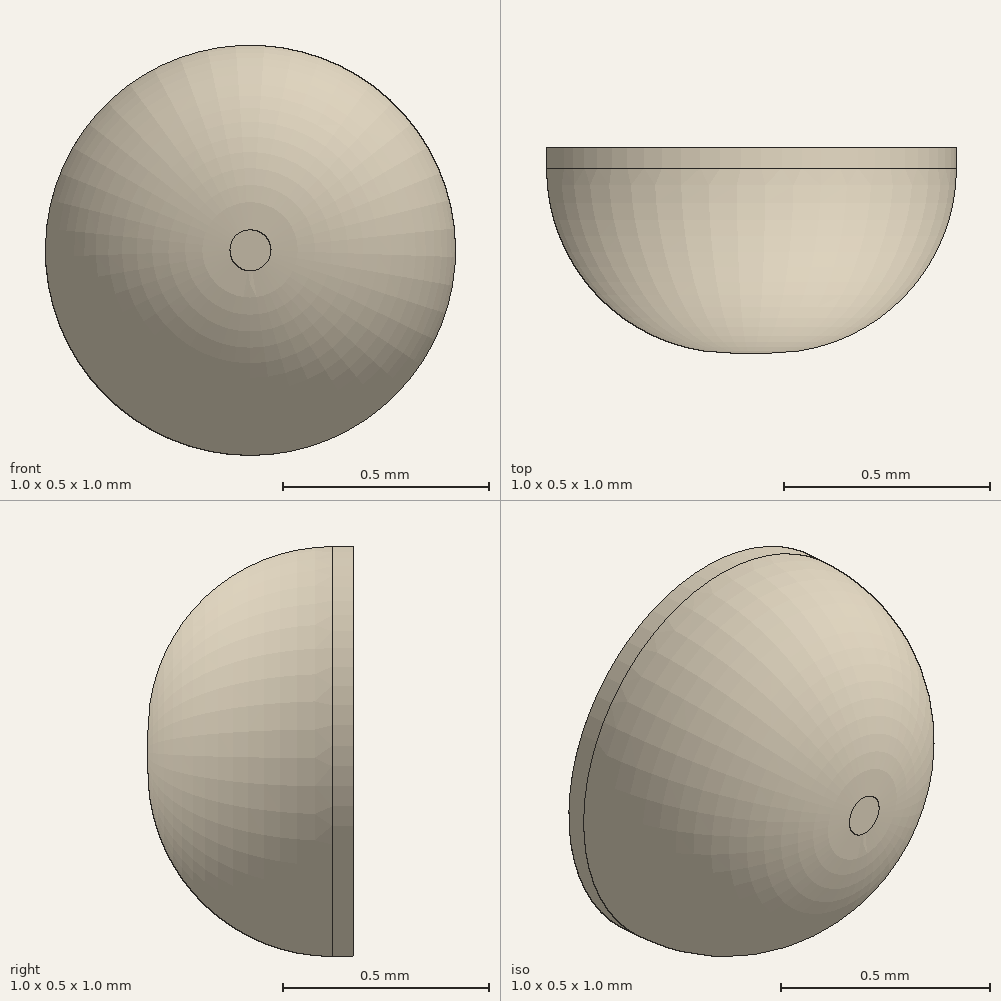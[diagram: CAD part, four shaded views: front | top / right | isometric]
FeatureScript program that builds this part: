
annotation { "Feature Type Name" : "Feature", "Feature Type Description" : "" }
export const myFeature = defineFeature(function(context is Context, id is Id, definition is map)
    precondition{}
    {
        {
            var Q0;
            Q0=qCreatedBy(makeId("Front.planeOp"),FACE);
            var sketch = newSketch(context, id + "F0", { "sketchPlane" : qUnion([Q0])});
            skCircle(sketch, "E0", {"center": v(0, 0) * mm, "radius": 0.5 * mm});
            skSolve(sketch);
        }
        {
            var Q0;
            Q0=makeQuery(id+"F0.imprint","IMPRINT",FACE,{"disambiguationData":[TD([[makeQuery(id+"F0.imprint","IMPRINT",EDGE,{"derivedFrom":sQuery(id+"F0.wireOp",EDGE,"E0")}),1.0]])]});
            extrude(context, id + "F1", {"entities" : qUnion([Q0]), "depth" : 0.5 * mm});
        }
        {
            var Q0;
            Q0=makeQuery(id+"F1.opExtrude","CAP_EDGE",EDGE,{"disambiguationData":[OSD([sQuery(id+"F0.wireOp",EDGE,"E0")])],"isStart":false});
            fillet(context, id + "F2", {"entities" : qUnion([Q0]), "radius" : 0.45 * mm, "allowEdgeOverflow" : false});
        }
    });
